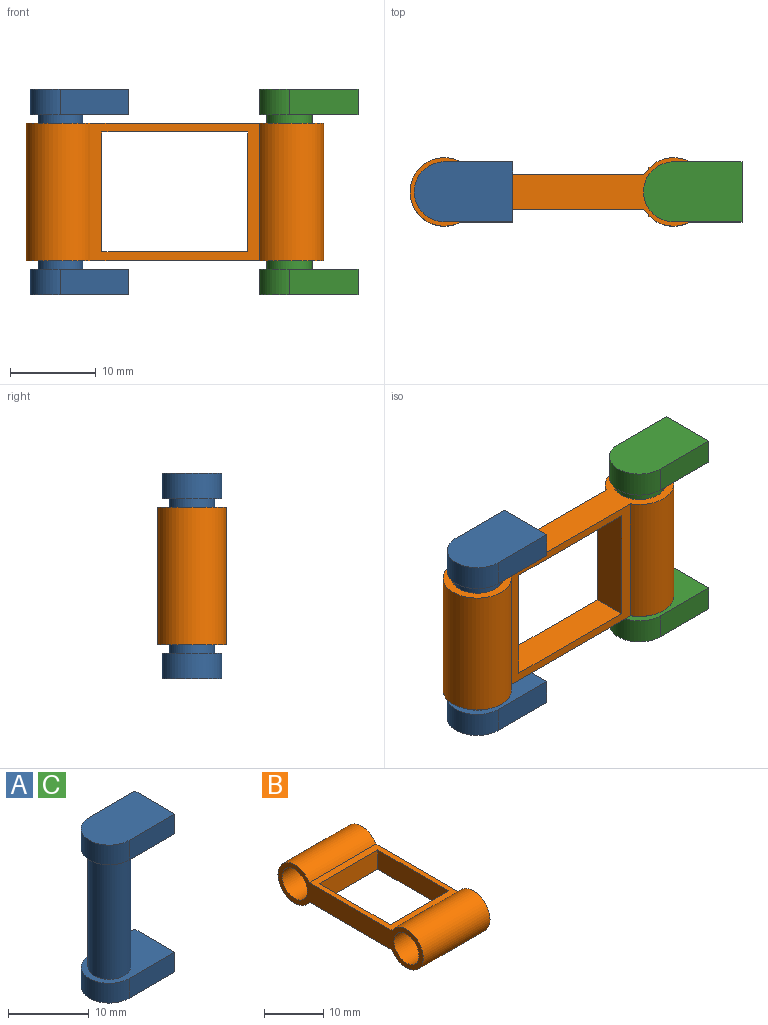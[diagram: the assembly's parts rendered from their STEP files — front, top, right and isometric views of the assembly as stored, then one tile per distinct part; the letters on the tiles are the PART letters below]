
ASSEMBLY  parts=3 mates=2
PART A: 13 faces, bbox 11.5x7x24 mm
  f0: cylinder r=2.65mm len=18mm, axis (0,0,1), area 299.7mm2, adj f3,f6
  f1: cylinder r=3.5mm len=7mm, axis (0,0,-1), area 33mm2, adj f2,f3,f7,f8
  f2: plane 11.5x7mm, normal (0,0,1), area 75.2mm2, adj f1,f7,f8,f9
  f3: plane 11.5x7mm, normal (0,0,-1), area 53.2mm2, adj f0,f1,f7,f8,f9
  f4: cylinder r=3.5mm len=7mm, axis (0,0,1), area 33mm2, adj f5,f6,f10,f11
  f5: plane 11.5x7mm, normal (0,0,-1), area 75.2mm2, adj f4,f10,f11,f12
  f6: plane 11.5x7mm, normal (0,0,1), area 53.2mm2, adj f0,f4,f10,f11,f12
  f7: plane 8x3mm, normal (0,1,0), area 24mm2, adj f1,f2,f3,f9
  f8: plane 8x3mm, normal (0,-1,0), area 24mm2, adj f1,f2,f3,f9
  f9: plane 7x3mm, normal (1,0,0), area 21mm2, adj f2,f3,f7,f8
  f10: plane 8x3mm, normal (0,-1,0), area 24mm2, adj f4,f5,f6,f12
  f11: plane 8x3mm, normal (0,1,0), area 24mm2, adj f4,f5,f6,f12
  f12: plane 7x3mm, normal (1,0,0), area 21mm2, adj f5,f6,f10,f11
PART B: 12 faces, bbox 16x34.8x8 mm
  f0: plane 17x4mm, normal (1,0,0), area 68mm2, adj f1,f5,f6,f7
  f1: plane 14x4mm, normal (0,-1,0), area 56mm2, adj f0,f2,f6,f7
  f2: plane 17x4mm, normal (-1,0,0), area 68mm2, adj f1,f5,f6,f7
  f3: plane 34.77x8mm, normal (-1,0,0), area 120.4mm2, adj f6,f7,f8,f9,f10,f11
  f4: plane 34.77x8mm, normal (1,0,0), area 120.4mm2, adj f6,f7,f8,f9,f10,f11
  f5: plane 14x4mm, normal (0,1,0), area 56mm2, adj f0,f2,f6,f7
  f6: plane 19.84x16mm, normal (0,0,-1), area 79.4mm2, adj f0,f1,f2,f3,f4,f5,f8,f9
  f7: plane 19.84x16mm, normal (0,0,1), area 79.4mm2, adj f0,f1,f2,f3,f4,f5,f8,f9
  f8: cylinder r=4mm len=16mm, axis (-1,0,0), area 335.1mm2, adj f3,f4,f6,f7
  f9: cylinder r=4mm len=16mm, axis (-1,0,0), area 335.1mm2, adj f3,f4,f6,f7
  f10: cylinder r=3mm len=16mm, axis (1,0,0), area 301.6mm2, adj f3,f4
  f11: cylinder r=3mm len=16mm, axis (1,0,0), area 301.6mm2, adj f3,f4
PART C: same geometry as A
PLACE A t=(-8.35,-2.34,8.93)mm
PLACE B rot(axis=(0.58,-0.58,0.58),120deg) t=(3.25,-4.34,3.93)mm
PLACE C t=(18.42,-2.34,8.93)mm
MATE revolute C.f0 <-> B.f9  axis (0,0,1) through (18.42,-2.34,-0.07)mm
MATE revolute B.f10 <-> A.f0  axis (0,0,1) through (-8.35,-2.34,-0.07)mm
